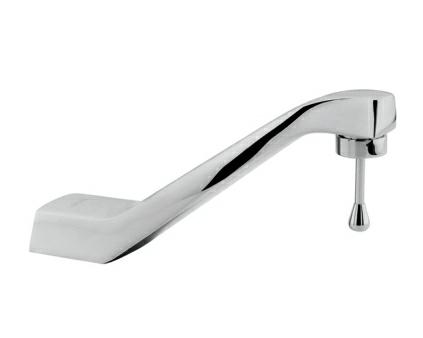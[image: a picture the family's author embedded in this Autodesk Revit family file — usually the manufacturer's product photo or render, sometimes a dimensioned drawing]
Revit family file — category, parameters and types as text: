
# Revit family: Llave Economizadora TV-105
name_source: partatom
category: Plumbing Fixtures
revit_build: Autodesk Revit 2015 (Build: 20140223_1515(x64)
units: mm (PartAtom-declared; Revit-internal decimal feet)

## types (1)
- TV-105
    Accessories = Economizador para autoajuste de flujo y palanca con recubrimiento antibacterial
    Chrome = Brass Chromed
    Compliance = NMX-C-415-ONNCCE-1999
    Connection = ½" - 14 NPSM
    Default Elevation = 48"
    Description = Llave Economizadora con Seguro Antirrobo
    Elevación por Defecto = 1"
    Manufacturer = HELVEX S.A. DE C.V.
    Max. Water Flow = 1.2 gal/min
    Max. Working Pressure = 85.3 psi
    Min. Working Pressure = 3.6 psi
    Model = TV-105
    Operation = Cierre Automático y Perilla multidireccional
    Total Height = 4"
    Total Length = 6"
    Total Width = 2"
    Type Comments = Llave Economizadora
    Type Image = TV-105.jpg
    URL = http://www.helvex.com.mx
    Warranty = El producto HELVEX está garantizado como libre de defectos en materiales y procesos de fabricación. El producto HELVEX está garantizado, en lo que se refiere a los acabados; por un periodo de 10 años en los acabados cromo y duravex, y por 2 años en cabados diferentes al cromo, a partir de la fecha de compra indicada en la factura.

## geometry (parser evidence)
native form markers: Sweep x3
no freeform markers — native parametric forms only
